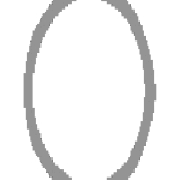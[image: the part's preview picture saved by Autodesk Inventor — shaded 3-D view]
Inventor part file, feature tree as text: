
AUTODESK INVENTOR PART (.ipt)
format: ipt  version: 2021 (Build 250183000, 183)  size: 136,704 bytes
history: native  units: in
note: dims shown in document units (in); Inventor stores cm internally (conversion verified against a paired STEP export)
features: plane x7, sketch x5, other x4, extrude x2, boolean_combine x2
ambient origin geometry x8: Origin, YZ Plane, XZ Plane, XY Plane, X Axis, Y Axis, Z Axis, Center Point
bodies: Solid1 (feature_tree), Body (feature_tree), Solid2 (feature_tree), Solid3 (feature_tree)
feature tree (20):
  other  "Driven Length"
  other  "Frame Generator"
  other  "Start Plane"
  other  "End Plane"
  plane  "Work Plane4"
  plane  "Work Plane5"
  plane  "Work Plane6"
  extrude  "Extrusion3"  Depth=0.065in
  boolean_combine  "Combine1"
  plane  "Work Plane7"
  plane  "Work Plane8"
  plane  "Work Plane9"
  extrude  "Extrusion4"  TaperAngle=0.0deg  [1 undecoded]
  boolean_combine  "Combine2"
  sketch  "Sketch"  dims[d8=90.0deg d9=20.0in d10=0.12in d11=0.0in d12=0.12in d13=0.0in]
  sketch  "Sketch2"  dims[d0=1.0in d1=0.065in]
  plane  "Work Plane3"
  sketch  "Sketch3"  dims[d2=20.0in d4=-0.0in]
  sketch  "Sketch4"  dims[d5=20.0in]
  sketch  "Sketch5"  dims[d6=0.12in d7=0.0in]
note: 1 required parameter value undecoded (feature->parameter linkage not recoverable at this tier; creation-order binding heuristic only, values carry confidence <= 0.55)
